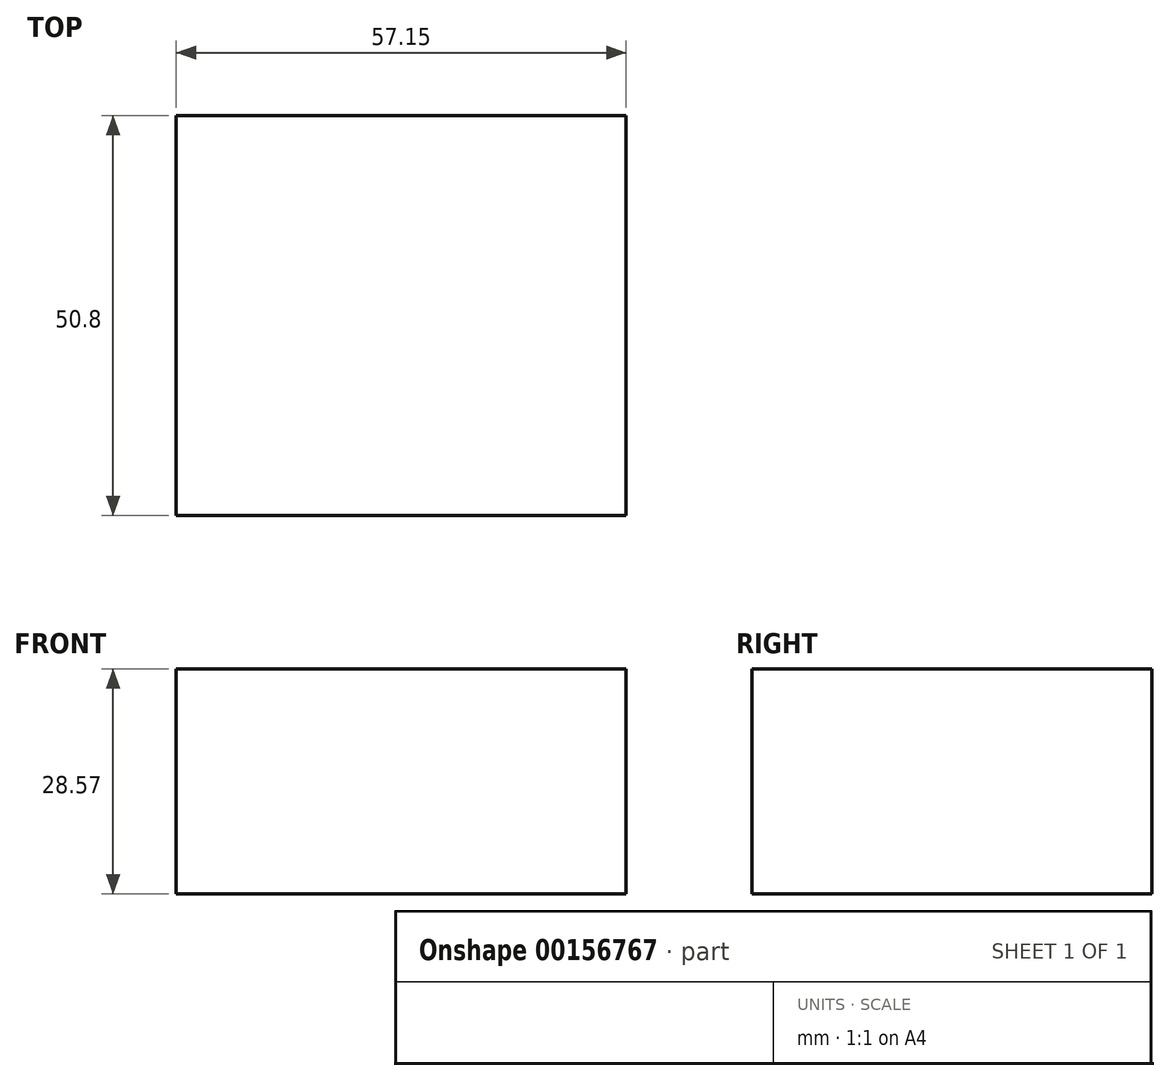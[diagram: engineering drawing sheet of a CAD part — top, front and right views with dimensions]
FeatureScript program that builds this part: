
annotation { "Feature Type Name" : "Feature", "Feature Type Description" : "" }
export const myFeature = defineFeature(function(context is Context, id is Id, definition is map)
    precondition{}
    {
        {
            var Q0;
            Q0=qCreatedBy(makeId("Front.planeOp"),FACE);
            var sketch = newSketch(context, id + "F0", { "sketchPlane" : qUnion([Q0])});
            skLineSegment(sketch, "E0.bottom", {"start": v(0, 0) * mm, "end": v(57.15, 0) * mm});
            skLineSegment(sketch, "E0.top", {"start": v(0, 28.58) * mm, "end": v(57.15, 28.58) * mm});
            skLineSegment(sketch, "E0.left", {"start": v(0, 0) * mm, "end": v(0, 28.58) * mm});
            skLineSegment(sketch, "E0.right", {"start": v(57.15, 0) * mm, "end": v(57.15, 28.58) * mm});
            skSolve(sketch);
        }
        {
            var Q0;
            Q0=makeQuery(id+"F0.imprint","IMPRINT",FACE,{"disambiguationData":[TD([[makeQuery(id+"F0.imprint","IMPRINT",EDGE,{"derivedFrom":sQuery(id+"F0.wireOp",EDGE,"E0.bottom")}),1.0]])]});
            extrude(context, id + "F1", {"entities" : qUnion([Q0]), "depth" : 50.8 * mm});
        }
    });
